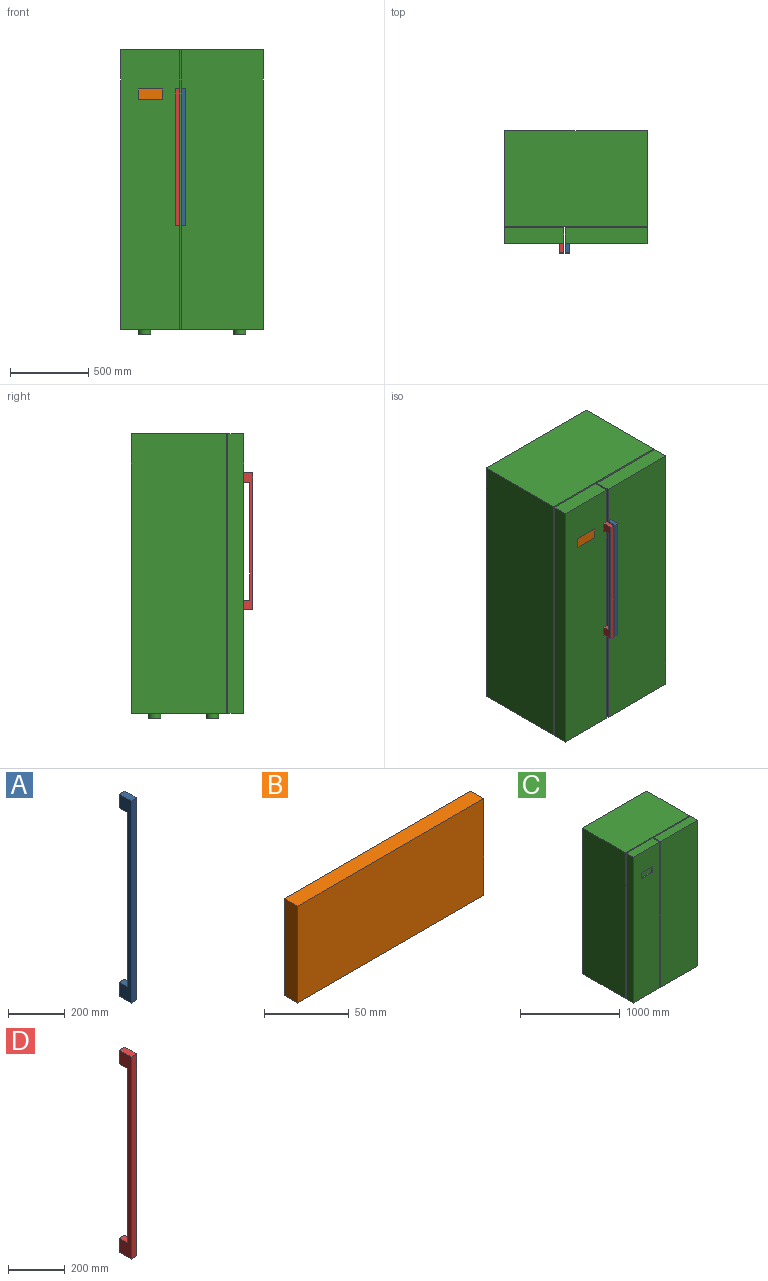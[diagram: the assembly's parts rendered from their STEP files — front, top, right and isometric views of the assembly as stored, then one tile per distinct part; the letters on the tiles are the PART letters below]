
ASSEMBLY  parts=4 mates=3
PART A: 10 faces, bbox 27x60x875 mm
  f0: plane 60x27mm, normal (0,1,0), area 1620mm2, adj f1,f2,f4,f7
  f1: plane 875x60mm, normal (-1,0,0), area 22300mm2, adj f0,f2,f3,f5,f6,f7,f8,f9
  f2: plane 60x27mm, normal (0,0,1), area 1620mm2, adj f0,f1,f4,f5
  f3: plane 60x27mm, normal (0,0,-1), area 1620mm2, adj f1,f4,f5,f6
  f4: plane 875x60mm, normal (1,0,0), area 22300mm2, adj f0,f2,f3,f5,f6,f7,f8,f9
  f5: plane 875x27mm, normal (0,-1,0), area 23625mm2, adj f1,f2,f3,f4
  f6: plane 60x27mm, normal (0,1,0), area 1620mm2, adj f1,f3,f4,f9
  f7: plane 40x27mm, normal (0,0,-1), area 1080mm2, adj f0,f1,f4,f8
  f8: plane 755x27mm, normal (0,1,0), area 20385mm2, adj f1,f4,f7,f9
  f9: plane 40x27mm, normal (0,0,1), area 1080mm2, adj f1,f4,f6,f8
PART B: 6 faces, bbox 156x11x70 mm
  f0: plane 156x11mm, normal (0,0,1), area 1716mm2, adj f1,f3,f4,f5
  f1: plane 70x11mm, normal (-1,0,0), area 770mm2, adj f0,f2,f4,f5
  f2: plane 156x11mm, normal (0,0,-1), area 1716mm2, adj f1,f3,f4,f5
  f3: plane 70x11mm, normal (1,0,0), area 770mm2, adj f0,f2,f4,f5
  f4: plane 156x70mm, normal (0,-1,0), area 10920mm2, adj f0,f1,f2,f3
  f5: plane 156x70mm, normal (0,1,0), area 10920mm2, adj f0,f1,f2,f3
PART C: 37 faces, bbox 910x720x1820 mm
  f0: plane 1790x375mm, normal (0,-1,0), area 660330mm2, adj f2,f6,f13,f30,f32,f33,f34,f35
  f1: plane 525x100mm, normal (0,0,1), area 52500mm2, adj f4,f14,f15,f31
  f2: plane 375x100mm, normal (0,0,-1), area 37500mm2, adj f0,f13,f26,f30
  f3: plane 515x10mm, normal (0,0,-1), area 5150mm2, adj f4,f27,f28,f31
  f4: plane 1790x525mm, normal (0,1,0), area 28200mm2, adj f1,f3,f5,f12,f15,f28,f31
  f5: plane 515x10mm, normal (0,0,1), area 5150mm2, adj f4,f27,f28,f31
  f6: plane 375x100mm, normal (0,0,1), area 37500mm2, adj f0,f13,f26,f30
  f7: plane 1770x10mm, normal (-1,0,0), area 17700mm2, adj f9,f26,f27,f29
  f8: plane 1790x610mm, normal (-1,0,0), area 1091900mm2, adj f10,f16,f21,f27
  f9: plane 365x10mm, normal (0,0,-1), area 3650mm2, adj f7,f26,f27,f30
  f10: plane 910x610mm, normal (0,0,1), area 555100mm2, adj f8,f11,f16,f27
  f11: plane 1790x610mm, normal (1,0,0), area 1091900mm2, adj f10,f16,f21,f27
  f12: plane 525x100mm, normal (0,0,-1), area 52500mm2, adj f4,f14,f15,f31
  f13: plane 1790x100mm, normal (-1,0,0), area 179000mm2, adj f0,f2,f6,f26
  f14: plane 1790x525mm, normal (0,-1,0), area 939750mm2, adj f1,f12,f15,f31
  f15: plane 1790x100mm, normal (1,0,0), area 179000mm2, adj f1,f4,f12,f14
  f16: plane 1790x910mm, normal (0,1,0), area 1628900mm2, adj f8,f10,f11,f21
  f17: cylinder r=40mm len=80mm, axis (0,0,-1), area 7539.8mm2, adj f21,f24
  f18: cylinder r=40mm len=80mm, axis (0,0,-1), area 7539.8mm2, adj f21,f23
  f19: cylinder r=40mm len=80mm, axis (0,0,-1), area 7539.8mm2, adj f21,f22
  f20: cylinder r=40mm len=80mm, axis (0,0,-1), area 7539.8mm2, adj f21,f25
  f21: plane 910x610mm, normal (0,0,-1), area 534993.8mm2, adj f8,f11,f16,f17,f18,f19,f20,f27
  f22: plane 80x80mm, normal (0,0,-1), area 5026.5mm2, adj f19
  f23: plane 80x80mm, normal (0,0,-1), area 5026.5mm2, adj f18
  f24: plane 80x80mm, normal (0,0,-1), area 5026.5mm2, adj f17
  f25: plane 80x80mm, normal (0,0,-1), area 5026.5mm2, adj f20
  f26: plane 1790x375mm, normal (0,1,0), area 25200mm2, adj f2,f6,f7,f9,f13,f29,f30
  f27: plane 1790x910mm, normal (0,-1,0), area 71300mm2, adj f3,f5,f7,f8,f9,f10,f11,f21
  f28: plane 1770x10mm, normal (1,0,0), area 17700mm2, adj f3,f4,f5,f27
  f29: plane 365x10mm, normal (0,0,1), area 3650mm2, adj f7,f26,f27,f30
  f30: plane 1790x110mm, normal (1,0,0), area 196700mm2, adj f0,f2,f6,f9,f26,f27,f29
  f31: plane 1790x110mm, normal (-1,0,0), area 196700mm2, adj f1,f3,f4,f5,f12,f14,f27
  f32: plane 156x10mm, normal (0,0,-1), area 1560mm2, adj f0,f33,f35,f36
  f33: plane 70x10mm, normal (1,0,0), area 700mm2, adj f0,f32,f34,f36
  f34: plane 156x10mm, normal (0,0,1), area 1560mm2, adj f0,f33,f35,f36
  f35: plane 70x10mm, normal (-1,0,0), area 700mm2, adj f0,f32,f34,f36
  f36: plane 156x70mm, normal (0,-1,0), area 10920mm2, adj f32,f33,f34,f35
PART D: 10 faces, bbox 27x60x875 mm
  f0: plane 60x27mm, normal (0,1,0), area 1620mm2, adj f1,f3,f4,f8
  f1: plane 875x60mm, normal (1,0,0), area 22300mm2, adj f0,f2,f4,f5,f6,f7,f8,f9
  f2: plane 60x27mm, normal (0,0,1), area 1620mm2, adj f1,f3,f5,f6
  f3: plane 875x60mm, normal (-1,0,0), area 22300mm2, adj f0,f2,f4,f5,f6,f7,f8,f9
  f4: plane 60x27mm, normal (0,0,-1), area 1620mm2, adj f0,f1,f3,f5
  f5: plane 875x27mm, normal (0,-1,0), area 23625mm2, adj f1,f2,f3,f4
  f6: plane 60x27mm, normal (0,1,0), area 1620mm2, adj f1,f2,f3,f7
  f7: plane 40x27mm, normal (0,0,-1), area 1080mm2, adj f1,f3,f6,f9
  f8: plane 40x27mm, normal (0,0,1), area 1080mm2, adj f0,f1,f3,f9
  f9: plane 755x27mm, normal (0,1,0), area 20385mm2, adj f1,f3,f7,f8
PLACE A t=(-378.17,233.3,-101.28)mm
PLACE B t=(-378.17,233.3,-101.28)mm
PLACE C t=(-378.17,233.3,-101.28)mm
PLACE D t=(-378.17,233.3,-101.28)mm
MATE fastened A.f2 <-> C.f32  axis (0,0,1) through (24.71,263.83,1468.72)mm
MATE fastened D.f2 <-> C.f32  axis (0,0,1) through (14.71,263.83,1468.72)mm
MATE fastened B.f0 <-> C.f32  axis (0,0,1) through (-172.79,262.83,1468.72)mm
